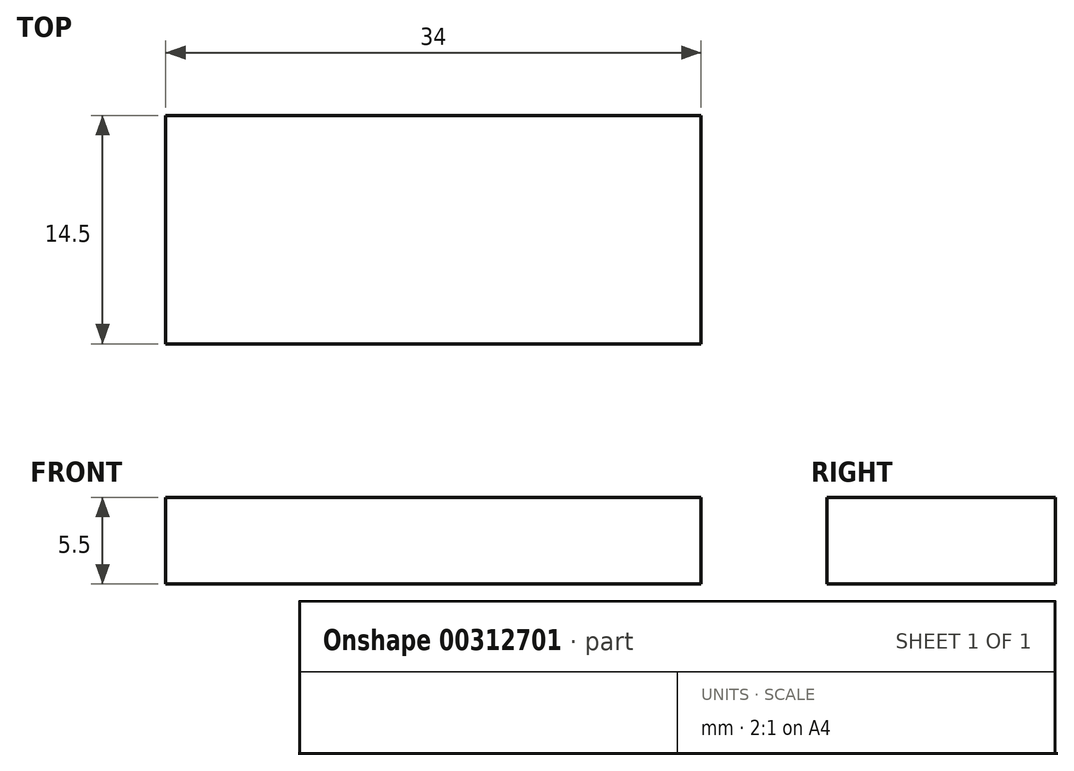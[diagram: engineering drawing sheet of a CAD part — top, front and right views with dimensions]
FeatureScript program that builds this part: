
annotation { "Feature Type Name" : "Feature", "Feature Type Description" : "" }
export const myFeature = defineFeature(function(context is Context, id is Id, definition is map)
    precondition{}
    {
        {
            var Q0;
            Q0=qCreatedBy(makeId("Top.planeOp"),FACE);
            var sketch = newSketch(context, id + "F0", { "sketchPlane" : qUnion([Q0])});
            skLineSegment(sketch, "E0.bottom", {"start": v(6.47, -22.42) * mm, "end": v(40.47, -22.42) * mm});
            skLineSegment(sketch, "E0.top", {"start": v(6.47, -36.92) * mm, "end": v(40.47, -36.92) * mm});
            skLineSegment(sketch, "E0.left", {"start": v(6.47, -22.42) * mm, "end": v(6.47, -36.92) * mm});
            skLineSegment(sketch, "E0.right", {"start": v(40.47, -22.42) * mm, "end": v(40.47, -36.92) * mm});
            skSolve(sketch);
        }
        {
            var Q0;
            Q0=makeQuery(id+"F0.imprint","IMPRINT",FACE,{"disambiguationData":[TD([[makeQuery(id+"F0.imprint","IMPRINT",EDGE,{"derivedFrom":sQuery(id+"F0.wireOp",EDGE,"E0.bottom")}),-1.0]])]});
            extrude(context, id + "F1", {"entities" : qUnion([Q0]), "depth" : 5.5 * mm});
        }
    });
